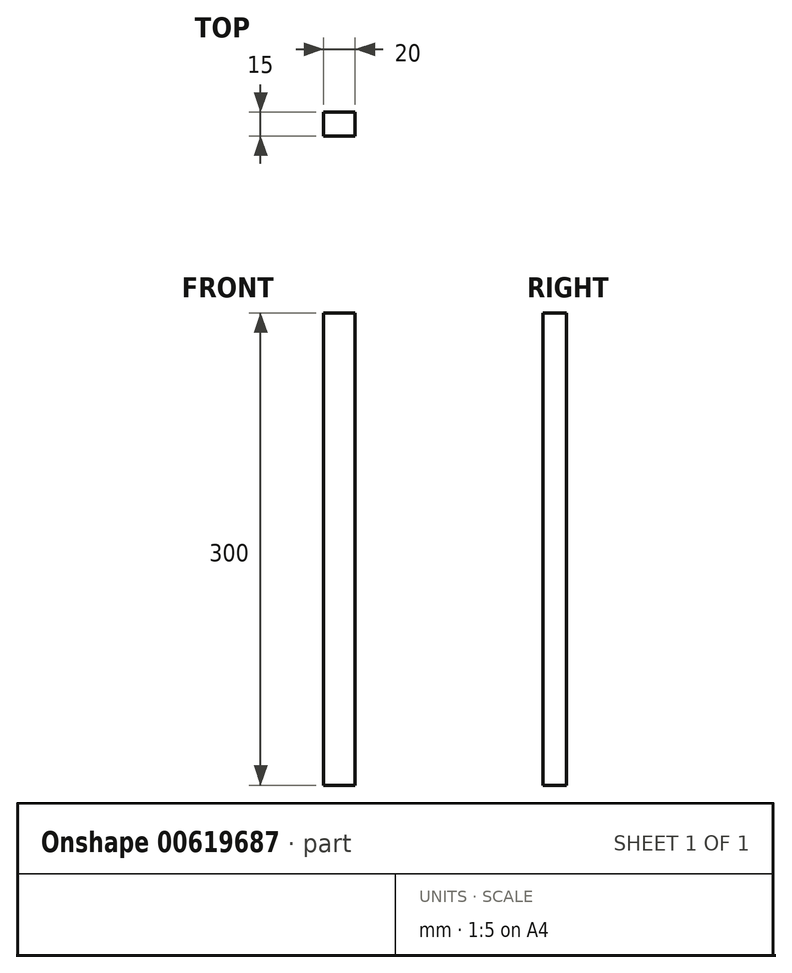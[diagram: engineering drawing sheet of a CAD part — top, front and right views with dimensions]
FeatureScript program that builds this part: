
annotation { "Feature Type Name" : "Feature", "Feature Type Description" : "" }
export const myFeature = defineFeature(function(context is Context, id is Id, definition is map)
    precondition{}
    {
        {
            var Q0;
            Q0=qCreatedBy(makeId("Top.planeOp"),FACE);
            var sketch = newSketch(context, id + "F0", { "sketchPlane" : qUnion([Q0])});
            skLineSegment(sketch, "E0.bottom", {"start": v(10, -7.5) * mm, "end": v(-10, -7.5) * mm});
            skLineSegment(sketch, "E0.top", {"start": v(10, 7.5) * mm, "end": v(-10, 7.5) * mm});
            skLineSegment(sketch, "E0.left", {"start": v(10, -7.5) * mm, "end": v(10, 7.5) * mm});
            skLineSegment(sketch, "E0.right", {"start": v(-10, -7.5) * mm, "end": v(-10, 7.5) * mm});
            skPoint(sketch, "E0.middle", {"position": v(0, 0) * mm});
            skSolve(sketch);
        }
        {
            var Q0;
            Q0 = qSketchRegion(id + "F0", true);
            extrude(context, id + "F1", {"entities" : qUnion([Q0]), "depth" : 300 * mm, "offsetDistance" : 25 * mm});
        }
    });
